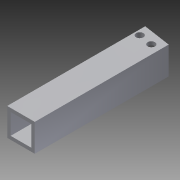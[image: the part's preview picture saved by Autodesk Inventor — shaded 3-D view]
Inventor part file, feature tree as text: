
AUTODESK INVENTOR PART (.ipt)
format: ipt  version: 2013 (Build 170138000, 138)  size: 97,792 bytes
history: native  units: in
note: dims shown in document units (in); Inventor stores cm internally (conversion verified against a paired STEP export)
features: extrude x3, sketch x3, reference x2
ambient origin geometry x8: Origin, YZ Plane, XZ Plane, XY Plane, X Axis, Y Axis, Z Axis, Center Point
bodies: Solid1 (feature_tree)
feature tree (8):
  extrude  "Extrusion1"  Depth=1.0in
  extrude  "Extrusion2"  Depth=5.0in TaperAngle=0.0deg
  extrude  "Extrusion3"  Depth=5.0in TaperAngle=0.0deg
  sketch  "Sketch1"  dims[d0=1.0in d1=1.0in]
  sketch  "Sketch2"  dims[d2=0.125in d3=5.0in d4=0.0in]
  sketch  "Sketch3"  dims[d5=0.0586in d6=5.0in d7=0.0in d8=2.5in d9=0.0in]
  reference  "Reference1"
  reference  "Reference2"
